# Revit family: Control_Panels-Lutron-Energi_Savr_Node-QSN2
name_source: partatom
category: Electrical Equipment
revit_build: Autodesk Revit 2018 (Build: 20170223_1515(x64)
units: mm (PartAtom-declared; Revit-internal decimal feet)

## family parameters
Cut with Voids When Loaded = No
Host = Face
OmniClass Number = 23.80.30.11.17
OmniClass Title = Distribution Boards and Control Panels
Panel Configuration = Two Columns, Circuits Across
Part Type = Panelboard
Room Calculation Point = No
Round Connector Dimension = Use Radius
Shared = No

## types (3) — shared parameters
Description = 0–10 V-/Softswitch 20 A Receptacle/Fixture Controllers
Finish = Steel - Lutron - Black
Frequency = 60 Hz
Ground Bus = No
Instruction Sheet Link = https://www.lutron.com
Load Classification = Power
MCB Rating = 1 A
Manufacturer = Lutron Electronics Co., Inc
Manufacturer Fax Number = 610-282-1243
Neutral Bus = No
Neutral Rating = 0.00%
Number of Poles = 1
Overall Depth = 3.14 "
Overall Height = 13.25 "
Overall Width = 9.25 "
Phase = 1
Power Factor = 1
Product Documentation Link = https://www.lutron.com
Product Name = Energi Savr Node
Product Page URL = https://www.lutron.com
Series = Athena
SubFeed Lugs = No
URL = http://www.lutron.com
Unit Weight = 0.00 lb
Version = 2018 - v1.0a
Video Link = https://www.youtube.com
Warranty URL = http://www.lutron.com
zero-valued in all types: Cost, Default Elevation

## per-type parameters (varying)
| type | Electrical Potential | Feed Through Control Circuit Load | Feed Through Control Circuit Voltage | Performance URL | Voltage |
| QSN2-4S20-S | 120 V | 2400 VA | 120 V | lutron.com/en-US/pages/supportcenter/support.aspx?productName=Athena&SECTION=Documents&PRDCMP=TRUE&ct=Performance%20Specifications | 120‑277 V~ |
| QSN2-4T20-S | 120 V | 2400 VA | 120 V | lutron.com/en-US/pages/supportcenter/support.aspx?productName=Athena&SECTION=Documents&PRDCMP=TRUE&ct=Performance%20Specifications | 120‑277 V~ |
| QSN2-4T16-S-347 | 347 V | 5552 VA | 347 V | https://www.lutron.com | 347 V~ |

note: column(s) folded — value = type name in every type: Model

## geometry (parser evidence)
native form markers: Sweep x2
no freeform markers — native parametric forms only
